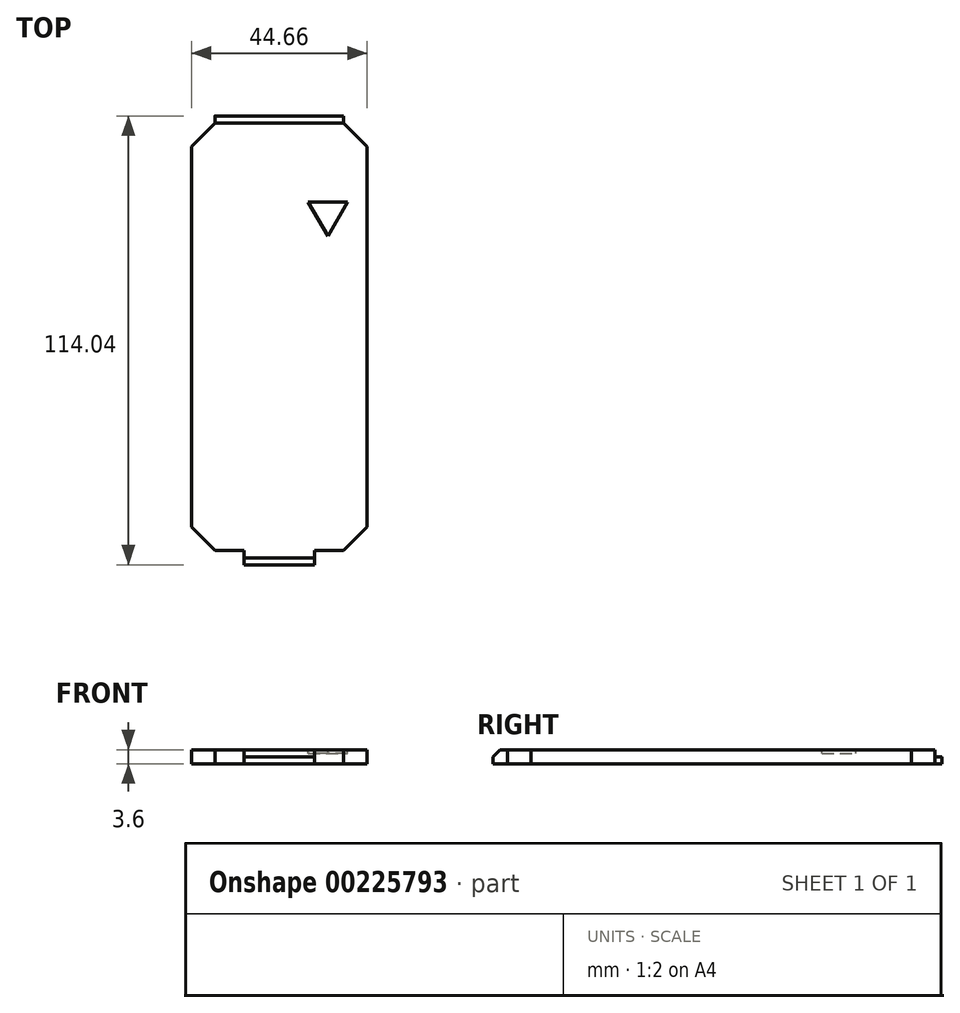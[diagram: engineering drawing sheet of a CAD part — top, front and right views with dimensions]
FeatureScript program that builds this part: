
annotation { "Feature Type Name" : "Feature", "Feature Type Description" : "" }
export const myFeature = defineFeature(function(context is Context, id is Id, definition is map)
    precondition{}
    {
        {
            assignVariable(context, id + "F0", {"name" : "O", "anyValue" : 3.6});
        }
        {
            var Q0;
            Q0=qCreatedBy(makeId("Top.planeOp"),FACE);
            var sketch = newSketch(context, id + "F1", { "sketchPlane" : qUnion([Q0])});
            skLineSegment(sketch, "E0.bottom", {"start": v(22.32, 54.33) * mm, "end": v(-22.33, 54.33) * mm});
            skLineSegment(sketch, "E0.top", {"start": v(22.33, -54.32) * mm, "end": v(-22.32, -54.32) * mm});
            skLineSegment(sketch, "E0.left", {"start": v(22.32, 54.33) * mm, "end": v(22.33, -54.32) * mm});
            skLineSegment(sketch, "E0.right", {"start": v(-22.33, 54.33) * mm, "end": v(-22.32, -54.32) * mm});
            skPoint(sketch, "E0.middle", {"position": v(0, 0) * mm});
            skSolve(sketch);
        }
        {
            var Q0;
            Q0=makeQuery(id+"F1.imprint","IMPRINT",FACE,{"disambiguationData":[TD([[makeQuery(id+"F1.imprint","IMPRINT",EDGE,{"derivedFrom":sQuery(id+"F1.wireOp",EDGE,"E0.bottom")}),1.0]])]});
            extrude(context, id + "F2", {"entities" : qUnion([Q0]), "depth" : (getVariable(context, 'O')) * mm});
        }
        {
            var Q0;
            Q0=makeQuery(id+"F2.opExtrude","SWEPT_EDGE",EDGE,{"disambiguationData":[OSD([sQuery(id+"F1.wireOp",EDGE,"E0.top"),sQuery(id+"F1.wireOp",EDGE,"E0.left")])]});
            var Q1;
            Q1=makeQuery(id+"F2.opExtrude","SWEPT_EDGE",EDGE,{"disambiguationData":[OSD([sQuery(id+"F1.wireOp",EDGE,"E0.top"),sQuery(id+"F1.wireOp",EDGE,"E0.right")])]});
            var Q2;
            Q2=makeQuery(id+"F2.opExtrude","SWEPT_EDGE",EDGE,{"disambiguationData":[OSD([sQuery(id+"F1.wireOp",EDGE,"E0.bottom"),sQuery(id+"F1.wireOp",EDGE,"E0.right")])]});
            var Q3;
            Q3=makeQuery(id+"F2.opExtrude","SWEPT_EDGE",EDGE,{"disambiguationData":[OSD([sQuery(id+"F1.wireOp",EDGE,"E0.bottom"),sQuery(id+"F1.wireOp",EDGE,"E0.left")])]});
            chamfer(context, id + "F3", {"entities" : qUnion([Q0, Q1, Q2, Q3]), "width" : (getVariable(context, 'O') * 1.67) * mm, "tangentPropagation" : true});
        }
        {
            var Q0;
            Q0=makeQuery(id+"F2.opExtrude","SWEPT_FACE",FACE,{"disambiguationData":[OSD([sQuery(id+"F1.wireOp",EDGE,"E0.bottom")])]});
            var sketch = newSketch(context, id + "F4", { "sketchPlane" : qUnion([Q0])});
            skLineSegment(sketch, "E1", {"start": v(-16.33, 1.8) * mm, "end": v(16.33, 1.8) * mm});
            skSolve(sketch);
        }
        {
            var Q0;
            {var subQ0=sQuery(id+"F4.wireOp",EDGE,"E1");Q0=makeQuery(id+"F4.imprint","IMPRINT",FACE,{"disambiguationData":[TD([[makeQuery(id+"F4.imprint","IMPRINT",EDGE,{"derivedFrom":subQ0}),-1.0]])]});}
            extrude(context, id + "F5", {"entities" : qUnion([Q0]), "operationType" : NewBodyOperationType.ADD, "depth" : (getVariable(context, 'O') / 2) * mm});
        }
        {
            var Q0;
            Q0=makeQuery(id+"F5.opExtrude","CAP_EDGE",EDGE,{"disambiguationData":[OSD([sQuery(id+"F4.wireOp",EDGE,"E1")])],"isStart":false});
            fillet(context, id + "F6", {"entities" : qUnion([Q0]), "radius" : .25 * mm, "tangentPropagation" : true, "allowEdgeOverflow" : false});
        }
        {
            var Q0;
            Q0=makeQuery(id+"F2.opExtrude","SWEPT_FACE",FACE,{"disambiguationData":[OSD([sQuery(id+"F1.wireOp",EDGE,"E0.top")])]});
            var sketch = newSketch(context, id + "F7", { "sketchPlane" : qUnion([Q0])});
            skLineSegment(sketch, "E2.bottom", {"start": v(9, 0) * mm, "end": v(-9, 0) * mm});
            skLineSegment(sketch, "E2.top", {"start": v(9, 3.6) * mm, "end": v(-9, 3.6) * mm});
            skLineSegment(sketch, "E2.left", {"start": v(9, 0) * mm, "end": v(9, 3.6) * mm});
            skLineSegment(sketch, "E2.right", {"start": v(-9, 0) * mm, "end": v(-9, 3.6) * mm});
            skPoint(sketch, "E2.middle", {"position": v(0, 1.8) * mm});
            skPoint(sketch, "E2.middle.positionSnap0", {"position": v(-16.33, 1.8) * mm});
            skPoint(sketch, "E2.centerSnap0", {"position": v(-16.33, 1.8) * mm});
            skSolve(sketch);
        }
        {
            var Q0;
            Q0=makeQuery(id+"F7.imprint","IMPRINT",FACE,{"disambiguationData":[TD([[makeQuery(id+"F7.imprint","IMPRINT",EDGE,{"derivedFrom":sQuery(id+"F7.wireOp",EDGE,"E2.bottom")}),-1.0]])]});
            extrude(context, id + "F8", {"entities" : qUnion([Q0]), "operationType" : NewBodyOperationType.ADD, "depth" : (getVariable(context, 'O')) * mm});
        }
        {
            var Q0;
            Q0=makeQuery(id+"F8.opExtrude","CAP_EDGE",EDGE,{"disambiguationData":[OSD([sQuery(id+"F7.wireOp",EDGE,"E2.top")])],"isStart":false});
            chamfer(context, id + "F9", {"entities" : qUnion([Q0]), "width" : (getVariable(context, 'O') / 2) * mm, "tangentPropagation" : true});
        }
        {
            var Q0;
            Q0=makeQuery(id+"F8.boolean.opBoolean","MERGE",FACE,{"derivedFrom":[makeQuery(id+"F2.opExtrude","CAP_FACE",FACE,{"disambiguationData":[OSD([sQuery(id+"F1.wireOp",EDGE,"E0.bottom"),sQuery(id+"F1.wireOp",EDGE,"E0.top"),sQuery(id+"F1.wireOp",EDGE,"E0.left"),sQuery(id+"F1.wireOp",EDGE,"E0.right")])],"isStart":false}),makeQuery(id+"F8.opExtrude","SWEPT_FACE",FACE,{"disambiguationData":[OSD([sQuery(id+"F7.wireOp",EDGE,"E2.top")])]})]});
            var sketch = newSketch(context, id + "F10", { "sketchPlane" : qUnion([Q0])});
            skPoint(sketch, "E3", {"position": v(12.32, 31.4) * mm});
            skCircle(sketch, "E4.cCircle", {"center": v(12.32, 31.4) * mm, "radius": 2.89 * mm, "construction": true});
            skLineSegment(sketch, "E4.0", {"start": v(7.32, 34.28) * mm, "end": v(17.32, 34.28) * mm});
            skLineSegment(sketch, "E4.1", {"start": v(17.32, 34.28) * mm, "end": v(12.32, 25.62) * mm});
            skLineSegment(sketch, "E4.2", {"start": v(12.32, 25.62) * mm, "end": v(7.33, 34.28) * mm});
            skPoint(sketch, "E4.0.midPoint", {"position": v(12.32, 34.28) * mm});
            skSolve(sketch);
        }
        {
            var Q0;
            Q0=makeQuery(id+"F10.imprint","IMPRINT",FACE,{"disambiguationData":[TD([[makeQuery(id+"F10.imprint","IMPRINT",EDGE,{"derivedFrom":sQuery(id+"F10.wireOp",EDGE,"E4.0")}),-1.0]])]});
            extrude(context, id + "F11", {"entities" : qUnion([Q0]), "operationType" : NewBodyOperationType.REMOVE, "oppositeDirection" : true, "depth" : (getVariable(context, 'O') / 4) * mm});
        }
    });
